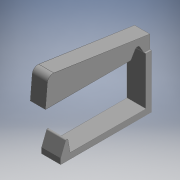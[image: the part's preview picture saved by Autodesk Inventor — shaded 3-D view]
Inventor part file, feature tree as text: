
AUTODESK INVENTOR PART (.ipt)
format: ipt  version: 2018 (Build 220112000, 112)  size: 158,208 bytes
history: native  units: mm
features: extrude x5, other x5, fillet x2
ambient origin geometry x8: Origin, YZ Plane, XZ Plane, XY Plane, X Axis, Y Axis, Z Axis, Center Point
bodies: Solid1 (feature_tree)
feature tree (12):
  extrude  "Key"  Depth=55.0mm
  fillet  "Key Front Rounding"  Radius=15.0mm
  extrude  "Downward Lever Section"  Depth=7.0mm
  extrude  "Horizontal Lever Section"  TaperAngle=0.0deg  [1 undecoded]
  extrude  "Hinge Cut"  Depth=3.0mm
  extrude  "Tube Pincher"  Depth=14.835299mm
  fillet  "Tube Pincher Rounding"  [1 undecoded]
  other  "Key Sketch"
  other  "Down Lever Sect Sketch"
  other  "Hinge Cut Sketch"
  other  "Horiz Lever Sect Sketch"
  other  "Tube Pincher Sketch"
note: 2 required parameter values undecoded (feature->parameter linkage not recoverable at this tier; creation-order binding heuristic only, values carry confidence <= 0.55)
